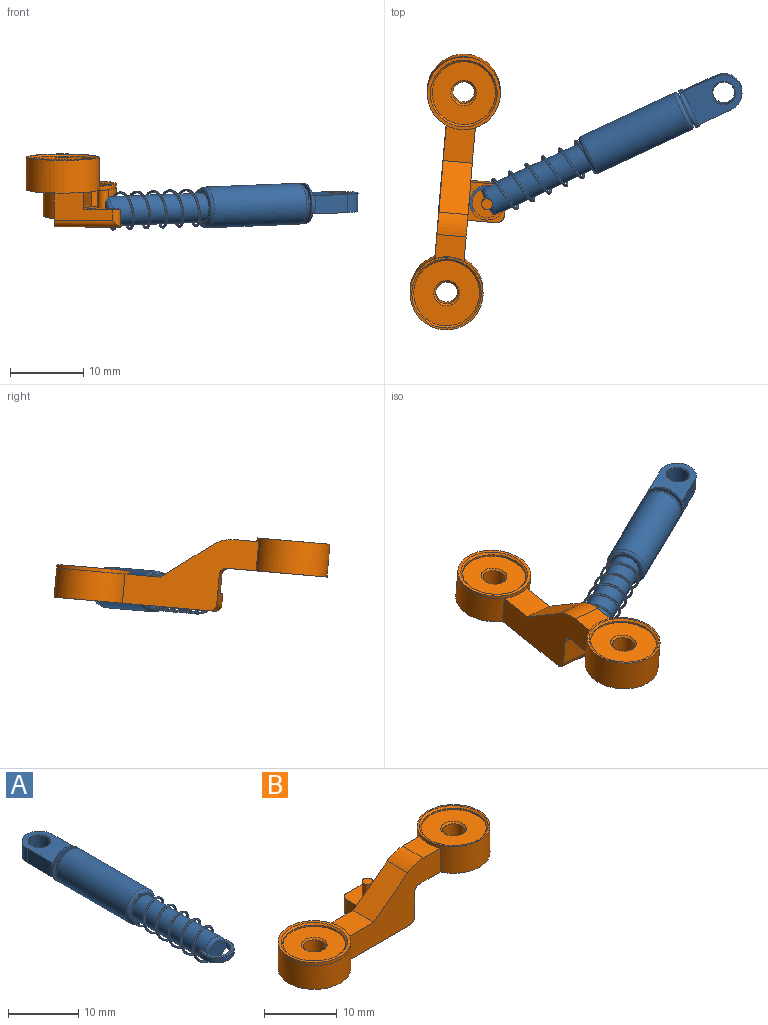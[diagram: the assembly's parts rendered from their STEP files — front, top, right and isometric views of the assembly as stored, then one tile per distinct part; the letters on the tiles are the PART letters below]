
ASSEMBLY  parts=2 mates=1
PART A: 37 faces, bbox 6.2x40.9x6.2 mm
  f0: cylinder r=2.8mm len=2.5mm, axis (0,1,0), area 1.3mm2, adj f5,f6,f7,f11
  f1: plane 5x2.5mm, normal (1,0,0), area 12.5mm2, adj f2,f5,f6,f7
  f2: cylinder r=2.5mm len=5mm, axis (0,0,-1), area 19.6mm2, adj f1,f3,f5,f6
  f3: plane 5x2.5mm, normal (-1,0,0), area 12.5mm2, adj f2,f5,f6,f12
  f4: cylinder r=1.5mm len=3mm, axis (0,0,-1), area 21.7mm2, adj f31,f32
  f5: plane 8.14x5.14mm, normal (0,0,1), area 26.9mm2, adj f0,f1,f2,f3,f8,f10,f30,f31
  f6: plane 8.14x5.14mm, normal (0,0,-1), area 26.9mm2, adj f0,f1,f2,f3,f9,f10,f29,f32
  f7: plane 2.5x0.3mm, normal (0,1,0), area 0.5mm2, adj f0,f1
  f8: plane 3.85x1.05mm, normal (0,1,0), area 2.8mm2, adj f5,f30
  f9: plane 3.85x1.05mm, normal (0,1,0), area 2.8mm2, adj f6,f29
  f10: cylinder r=2.8mm len=2.5mm, axis (0,1,0), area 1.3mm2, adj f5,f6,f11,f12
  f11: plane 5.59x5.59mm, normal (0,-1,0), area 8.6mm2, adj f0,f10,f13,f29,f30
  f12: plane 2.5x0.3mm, normal (0,1,0), area 0.5mm2, adj f3,f10
  f13: cylinder r=2.25mm len=4.5mm, axis (0,1,0), area 3.5mm2, adj f11,f16
  f14: cylinder r=2.8mm len=14mm, axis (0,1,0), area 245.9mm2, adj f27,f28
  f15: plane 4.59x4.59mm, normal (0,-1,0), area 4mm2, adj f19,f28
  f16: plane 4.59x4.59mm, normal (0,1,0), area 0.6mm2, adj f13,f27
  f17: plane 0.28x0.28mm, normal (0.06,0,1), area 0mm2, adj f18
  f18: bspline ~14.35x5.19mm, area 64.4mm2, adj f17,f28
  f19: cylinder r=2mm len=14.5mm, axis (0,1,0), area 180.1mm2, adj f15,f21,f22,f23,f25,f26,f34,f35
  f20: plane 4.05x3mm, normal (0,-1,0), area 8mm2, adj f22,f23,f24,f25,f26,f33,f36
  f21: cylinder r=2.49mm len=4.98mm, axis (0,0,1), area 8.8mm2, adj f19,f34,f35
  f22: plane 4.86x3.88mm, normal (0,0,-1), area 3.5mm2, adj f19,f20,f25,f33,f34
  f23: plane 4.86x3.88mm, normal (0,0,1), area 3.5mm2, adj f19,f20,f26,f35,f36
  f24: cylinder r=1.92mm len=3.85mm, axis (0,0,-1), area 4.8mm2, adj f20,f33,f36
  f25: torus R=1.5mm, axis (0,-1,0), area 3.6mm2, adj f19,f20,f22
  f26: torus R=1.5mm, axis (0,-1,0), area 3.6mm2, adj f19,f20,f23
  f27: torus R=2.3mm, axis (0,-1,0), area 12.9mm2, adj f14,f16
  f28: torus R=2.3mm, axis (0,-1,0), area 12.6mm2, adj f14,f15,f18
  f29: torus R=2.3mm, axis (0,-1,0), area 4.3mm2, adj f6,f9,f11
  f30: torus R=2.3mm, axis (0,-1,0), area 4.3mm2, adj f5,f8,f11
  f31: cone r=1.5mm half-angle=45deg, axis (0,0,1), area 1.4mm2, adj f4,f5
  f32: cone r=1.6mm half-angle=45deg, axis (0,0,-1), area 1.4mm2, adj f4,f6
  f33: cone r=1.92mm half-angle=45deg, axis (0,0,-1), area 0.9mm2, adj f20,f22,f24
  f34: cone r=2.39mm half-angle=45deg, axis (0,0,1), area 1.5mm2, adj f19,f21,f22
  f35: cone r=2.49mm half-angle=45deg, axis (0,0,-1), area 1.5mm2, adj f19,f21,f23
  f36: cone r=2.02mm half-angle=45deg, axis (0,0,1), area 0.9mm2, adj f20,f23,f24
PART B: 39 faces, bbox 37.1x12x10.5 mm
  f0: cylinder r=1.5mm len=3mm, axis (0,0,-1), area 28.3mm2, adj f29,f30
  f1: cylinder r=1.5mm len=3mm, axis (0,0,-1), area 28.3mm2, adj f28,f32
  f2: plane 9x9mm, normal (0,0,1), area 54mm2, adj f17,f30
  f3: plane 8x4mm, normal (1,0,0), area 22mm2, adj f6,f8,f25,f36,f37,f38
  f4: plane 8.66x8.66mm, normal (0,0,1), area 49.2mm2, adj f10,f32
  f5: plane 4.93x4.01mm, normal (0,0,1), area 18.6mm2, adj f6,f8,f11,f13
  f6: plane 17.92x10mm, normal (0,1,0), area 82.4mm2, adj f3,f5,f7,f9,f13,f14,f15,f16
  f7: cylinder r=5mm len=10mm, axis (0,0,-1), area 109.2mm2, adj f6,f8,f9,f11
  f8: plane 17.92x10mm, normal (0,-1,0), area 95.4mm2, adj f3,f5,f7,f9,f13,f14,f15,f16
  f9: plane 21.5x12mm, normal (0,0,-1), area 82.7mm2, adj f6,f7,f8,f19,f23,f24,f35,f36
  f10: cylinder r=4.33mm len=8.66mm, axis (0,0,-1), area 6.8mm2, adj f4,f33
  f11: cylinder r=5mm len=9.99mm, axis (0,0,-1), area 15.7mm2, adj f5,f7,f12
  f12: plane 9.99x9.99mm, normal (0,0,1), area 12.6mm2, adj f11,f33
  f13: plane 6.67x5mm, normal (-0.6,0,0.8), area 33.3mm2, adj f5,f6,f8,f34
  f14: cylinder r=5mm len=10mm, axis (0,0,-1), area 124.9mm2, adj f6,f8,f15,f16,f18
  f15: plane 4x3.33mm, normal (0,0,1), area 12.2mm2, adj f6,f8,f14,f34
  f16: plane 13.58x10mm, normal (0,0,-1), area 29.8mm2, adj f6,f8,f14,f21,f38
  f17: cylinder r=4.5mm len=9mm, axis (0,0,-1), area 7.1mm2, adj f2,f31
  f18: plane 10x10mm, normal (0,0,1), area 7.7mm2, adj f14,f31
  f19: cylinder r=4.5mm len=9mm, axis (0,0,-1), area 14.1mm2, adj f9,f20
  f20: plane 9x9mm, normal (0,0,-1), area 54mm2, adj f19,f28
  f21: cylinder r=4.5mm len=9mm, axis (0,0,-1), area 14.1mm2, adj f16,f22
  f22: plane 9x9mm, normal (0,0,-1), area 54mm2, adj f21,f29
  f23: plane 4x2.5mm, normal (-1,0,0), area 10mm2, adj f6,f9,f25,f35
  f24: plane 3.29x2.5mm, normal (0,1,0), area 8.2mm2, adj f9,f25,f35,f37
  f25: plane 5.29x5mm, normal (0,0,1), area 24.3mm2, adj f3,f6,f23,f24,f26,f35,f37
  f26: cylinder r=0.75mm len=2.5mm, axis (0,0,-1), area 11.8mm2, adj f25,f27
  f27: plane 1.5x1.5mm, normal (0,0,1), area 1.8mm2, adj f26
  f28: cone r=1.75mm half-angle=45deg, axis (0,0,-1), area 3.6mm2, adj f1,f20
  f29: cone r=1.75mm half-angle=45deg, axis (0,0,-1), area 3.6mm2, adj f0,f22
  f30: cone r=1.5mm half-angle=45deg, axis (0,0,1), area 3.6mm2, adj f0,f2
  f31: cone r=4.5mm half-angle=45deg, axis (0,0,1), area 10.3mm2, adj f17,f18
  f32: cone r=1.5mm half-angle=45deg, axis (0,0,1), area 3.6mm2, adj f1,f4
  f33: cone r=4.33mm half-angle=45deg, axis (0,0,1), area 9.9mm2, adj f10,f12
  f34: cylinder r=5mm len=4mm, axis (0,-1,0), area 12.9mm2, adj f6,f8,f13,f15
  f35: cylinder r=1mm len=2.5mm, axis (0,0,-1), area 3.9mm2, adj f9,f23,f24,f25
  f36: cylinder r=1mm len=9mm, axis (0,1,0), area 13.4mm2, adj f3,f8,f9,f37
  f37: cylinder r=1mm len=2.5mm, axis (0,0,1), area 3.1mm2, adj f3,f24,f25,f36
  f38: cylinder r=1mm len=4mm, axis (0,-1,0), area 6.3mm2, adj f3,f6,f8,f16
PLACE A rot(axis=(0.07,0.04,-1),65.2deg) t=(-4.03,-4.31,0.73)mm fixed
PLACE B rot(axis=(0.04,0.04,-1),95.1deg) t=(-20.75,-0.24,0.35)mm
MATE revolute A.f24 <-> B.f26  axis (0,-0.09,1) through (-17.56,-15.59,1.51)mm
